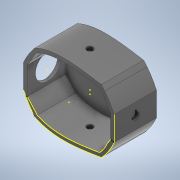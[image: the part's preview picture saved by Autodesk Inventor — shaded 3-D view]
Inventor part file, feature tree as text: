
AUTODESK INVENTOR PART (.ipt)
format: ipt  version: 2021.1 (Build 251245010, 245A)  size: 254,464 bytes
history: native  units: mm
features: sketch x5, extrude x5, plane x4, mirror x1
ambient origin geometry x8: Origin, YZ Plane, XZ Plane, XY Plane, X Axis, Y Axis, Z Axis, Center Point
bodies: Solid1 (feature_tree)
feature tree (15):
  sketch  "Sketch1"  dims[d1=70.0mm d2=70.0mm]
  sketch  "Sketch2"  dims[d3=0.0mm d4=6.0mm]
  extrude  "Extrusion1"  Depth=70.0mm
  extrude  "Extrusion2"  Depth=6.0mm
  plane  "Work Plane1"
  extrude  "Extrusion3"  TaperAngle=0.0deg  [1 undecoded]
  plane  "Work Plane2"
  sketch  "Sketch5"  dims[d5=64.0mm d6=0.0mm]
  mirror  "Mirror1"
  plane  "Work Plane3"
  extrude  "Extrusion4"  Depth=30.0mm TaperAngle=0.0deg
  plane  "Work Plane4"
  sketch  "Sketch6"  dims[d7=60.0mm d9=30.0mm d10=0.0mm]
  extrude  "Extrusion5"  Depth=49.152mm
  sketch  "Sketch7"  dims[d11=49.151954mm d12=49.152mm d13=10.0mm d14=10.0mm d15=20.0mm d16=0.0mm d19=40.0mm d20=6.0mm d21=6.0mm d22=35.0mm d23=15.0mm d24=0.0mm]
note: 1 required parameter value undecoded (feature->parameter linkage not recoverable at this tier; creation-order binding heuristic only, values carry confidence <= 0.55)
